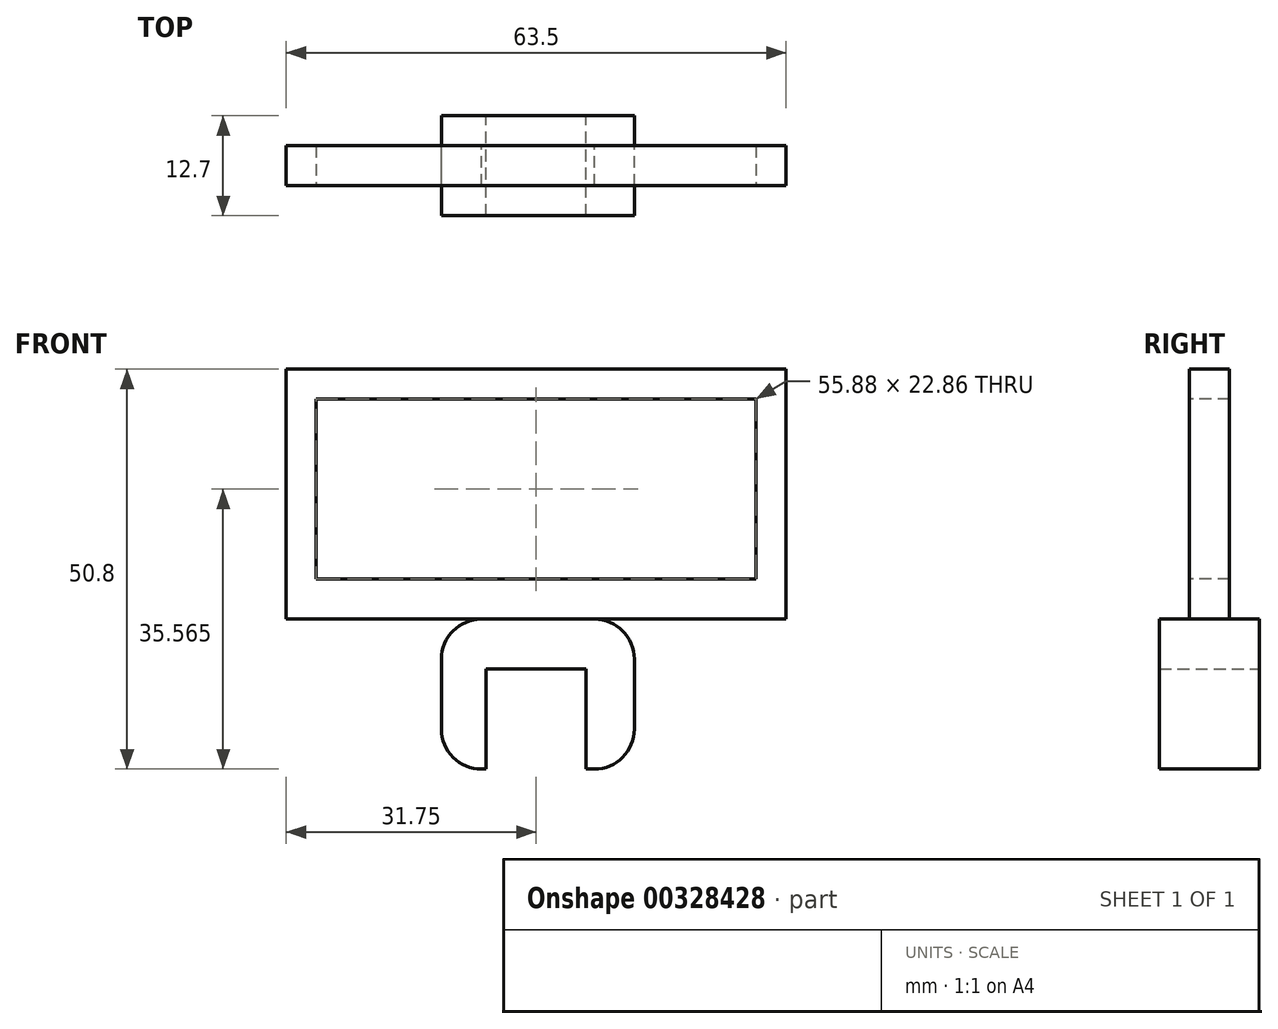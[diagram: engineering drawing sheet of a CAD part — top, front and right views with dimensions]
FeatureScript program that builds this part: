
annotation { "Feature Type Name" : "Feature", "Feature Type Description" : "" }
export const myFeature = defineFeature(function(context is Context, id is Id, definition is map)
    precondition{}
    {
        {
            var Q0;
            Q0=qCreatedBy(makeId("Front.planeOp"),FACE);
            var sketch = newSketch(context, id + "F0", { "sketchPlane" : qUnion([Q0])});
            skLineSegment(sketch, "E0.bottom", {"start": v(-6.35, 3.17) * mm, "end": v(6.35, 3.17) * mm});
            skLineSegment(sketch, "E0.top", {"start": v(-6.35, -3.18) * mm, "end": v(6.35, -3.18) * mm});
            skLineSegment(sketch, "E0.left", {"start": v(-6.35, 3.17) * mm, "end": v(-6.35, -3.18) * mm});
            skLineSegment(sketch, "E0.right", {"start": v(6.35, 3.18) * mm, "end": v(6.35, -3.18) * mm});
            skPoint(sketch, "E0.middle", {"position": v(0, 0) * mm});
            skLineSegment(sketch, "E1.bottom", {"start": v(-6.35, 3.17) * mm, "end": v(-12.05, 3.17) * mm});
            skLineSegment(sketch, "E1.top", {"start": v(-6.35, -15.88) * mm, "end": v(-12.05, -15.88) * mm});
            skLineSegment(sketch, "E1.left", {"start": v(-6.35, 3.17) * mm, "end": v(-6.35, -15.88) * mm});
            skLineSegment(sketch, "E1.right", {"start": v(-12.05, 3.17) * mm, "end": v(-12.05, -15.88) * mm});
            skLineSegment(sketch, "E2.bottom", {"start": v(6.35, 3.17) * mm, "end": v(12.46, 3.17) * mm});
            skLineSegment(sketch, "E2.top", {"start": v(6.35, -15.88) * mm, "end": v(12.46, -15.88) * mm});
            skLineSegment(sketch, "E2.left", {"start": v(6.35, 3.17) * mm, "end": v(6.35, -15.88) * mm});
            skLineSegment(sketch, "E2.right", {"start": v(12.46, 3.17) * mm, "end": v(12.46, -15.88) * mm});
            skSolve(sketch);
        }
        {
            var Q0;
            {var subQ3=sQuery(id+"F0.wireOp",EDGE,"E1.bottom");Q0=makeQuery(id+"F0.imprint","IMPRINT",FACE,{"disambiguationData":[TD([[makeQuery(id+"F0.imprint","IMPRINT",EDGE,{"derivedFrom":subQ3}),1.0]])]});}
            var Q1;
            {var subQ0=sQuery(id+"F0.wireOp",EDGE,"E0.bottom");Q1=makeQuery(id+"F0.imprint","IMPRINT",FACE,{"disambiguationData":[TD([[makeQuery(id+"F0.imprint","IMPRINT",EDGE,{"derivedFrom":subQ0}),-1.0]])]});}
            var Q2;
            {var subQ3=sQuery(id+"F0.wireOp",EDGE,"E2.bottom");Q2=makeQuery(id+"F0.imprint","IMPRINT",FACE,{"disambiguationData":[TD([[makeQuery(id+"F0.imprint","IMPRINT",EDGE,{"derivedFrom":subQ3}),-1.0]])]});}
            extrude(context, id + "F1", {"entities" : qUnion([Q0, Q1, Q2]), "depth" : 12.7 * mm});
        }
        {
            var Q0;
            Q0=makeQuery(id+"F1.opExtrude","SWEPT_EDGE",EDGE,{"disambiguationData":[OSD([sQuery(id+"F0.wireOp",EDGE,"E1.bottom"),sQuery(id+"F0.wireOp",EDGE,"E1.right")])]});
            var Q1;
            Q1=makeQuery(id+"F1.opExtrude","SWEPT_EDGE",EDGE,{"disambiguationData":[OSD([sQuery(id+"F0.wireOp",EDGE,"E2.bottom"),sQuery(id+"F0.wireOp",EDGE,"E2.right")])]});
            var Q2;
            Q2=makeQuery(id+"F1.opExtrude","SWEPT_EDGE",EDGE,{"disambiguationData":[OSD([sQuery(id+"F0.wireOp",EDGE,"E1.top"),sQuery(id+"F0.wireOp",EDGE,"E1.right")])]});
            var Q3;
            Q3=makeQuery(id+"F1.opExtrude","SWEPT_EDGE",EDGE,{"disambiguationData":[OSD([sQuery(id+"F0.wireOp",EDGE,"E2.top"),sQuery(id+"F0.wireOp",EDGE,"E2.right")])]});
            fillet(context, id + "F2", {"entities" : qUnion([Q0, Q1, Q2, Q3]), "radius" : 5.08 * mm, "tangentPropagation" : true, "allowEdgeOverflow" : false});
        }
        {
            var Q0;
            Q0=makeQuery(id+"F1.opExtrude","SWEPT_FACE",FACE,{"disambiguationData":[OSD([sQuery(id+"F0.wireOp",EDGE,"E0.bottom"),sQuery(id+"F0.wireOp",EDGE,"E1.bottom"),sQuery(id+"F0.wireOp",EDGE,"E2.bottom")])]});
            var sketch = newSketch(context, id + "F3", { "sketchPlane" : qUnion([Q0])});
            skLineSegment(sketch, "E3.bottom", {"start": v(-31.75, -3.8) * mm, "end": v(31.75, -3.8) * mm});
            skLineSegment(sketch, "E3.top", {"start": v(-31.75, -8.89) * mm, "end": v(31.75, -8.89) * mm});
            skLineSegment(sketch, "E3.left", {"start": v(-31.75, -3.8) * mm, "end": v(-31.75, -8.89) * mm});
            skLineSegment(sketch, "E3.right", {"start": v(31.75, -3.8) * mm, "end": v(31.75, -8.89) * mm});
            skPoint(sketch, "E3.middle", {"position": v(0, -6.35) * mm});
            skSolve(sketch);
        }
        {
            var Q0;
            {var subQ0=sQuery(id+"F3.wireOp",EDGE,"E3.left");Q0=makeQuery(id+"F3.imprint","IMPRINT",FACE,{"disambiguationData":[TD([[makeQuery(id+"F3.imprint","IMPRINT",EDGE,{"derivedFrom":subQ0}),1.0]])]});}
            var Q1;
            {var subQ0=sQuery(id+"F3.wireOp",EDGE,"E3.right");Q1=makeQuery(id+"F3.imprint","IMPRINT",FACE,{"disambiguationData":[TD([[makeQuery(id+"F3.imprint","IMPRINT",EDGE,{"derivedFrom":subQ0}),-1.0]])]});}
            var Q2;
            {var subQ0=sQuery(id+"F3.wireOp",EDGE,"E3.bottom");var subQ1=sQuery(id+"F0.wireOp",EDGE,"E2.bottom");var subQ2=sQuery(id+"F0.wireOp",EDGE,"E1.bottom");var subQ3=makeQuery(id+"F1.opExtrude","SWEPT_FACE",FACE,{"disambiguationData":[OSD([sQuery(id+"F0.wireOp",EDGE,"E0.bottom"),subQ2,subQ1])]});var subQ4=makeQuery(id+"F2.opFillet","BLEND_EDGE",EDGE,{"blendedFrom":[makeQuery(id+"F1.opExtrude","SWEPT_EDGE",EDGE,{"disambiguationData":[OSD([subQ2,sQuery(id+"F0.wireOp",EDGE,"E1.right")])]}),subQ3],"blendedInto":[subQ3]});var subQ5=makeQuery(id+"F3.imprint","INTERSECT",VERTEX,{"derivedFrom":[subQ4,subQ0]});Q2=makeQuery(id+"F3.imprint","IMPRINT",FACE,{"disambiguationData":[TD([[makeQuery(id+"F3.imprint","IMPRINT",EDGE,{"disambiguationData":[TD([[subQ5,-1.0]])],"derivedFrom":subQ0}),-1.0]])]});}
            extrude(context, id + "F4", {"entities" : qUnion([Q0, Q1, Q2]), "operationType" : NewBodyOperationType.ADD, "depth" : 31.75 * mm});
        }
        {
            var Q0;
            Q0=makeQuery(id+"F4.opExtrude","SWEPT_FACE",FACE,{"disambiguationData":[OSD([sQuery(id+"F3.wireOp",EDGE,"E3.top")])]});
            var sketch = newSketch(context, id + "F5", { "sketchPlane" : qUnion([Q0])});
            skPoint(sketch, "E4.middle", {"position": v(0, 20.96) * mm});
            skLineSegment(sketch, "E5.bottom", {"start": v(-27.94, 31.11) * mm, "end": v(27.94, 31.11) * mm});
            skLineSegment(sketch, "E5.top", {"start": v(-27.94, 8.26) * mm, "end": v(27.94, 8.26) * mm});
            skLineSegment(sketch, "E5.left", {"start": v(-27.94, 31.11) * mm, "end": v(-27.94, 8.26) * mm});
            skLineSegment(sketch, "E5.right", {"start": v(27.94, 31.11) * mm, "end": v(27.94, 8.26) * mm});
            skSolve(sketch);
        }
        {
            var Q0;
            Q0=makeQuery(id+"F5.imprint","IMPRINT",FACE,{"disambiguationData":[TD([[makeQuery(id+"F5.imprint","IMPRINT",EDGE,{"derivedFrom":sQuery(id+"F5.wireOp",EDGE,"E5.bottom")}),-1.0]])]});
            extrude(context, id + "F6", {"entities" : qUnion([Q0]), "operationType" : NewBodyOperationType.REMOVE, "oppositeDirection" : true, "depth" : 25.4 * mm});
        }
    });
